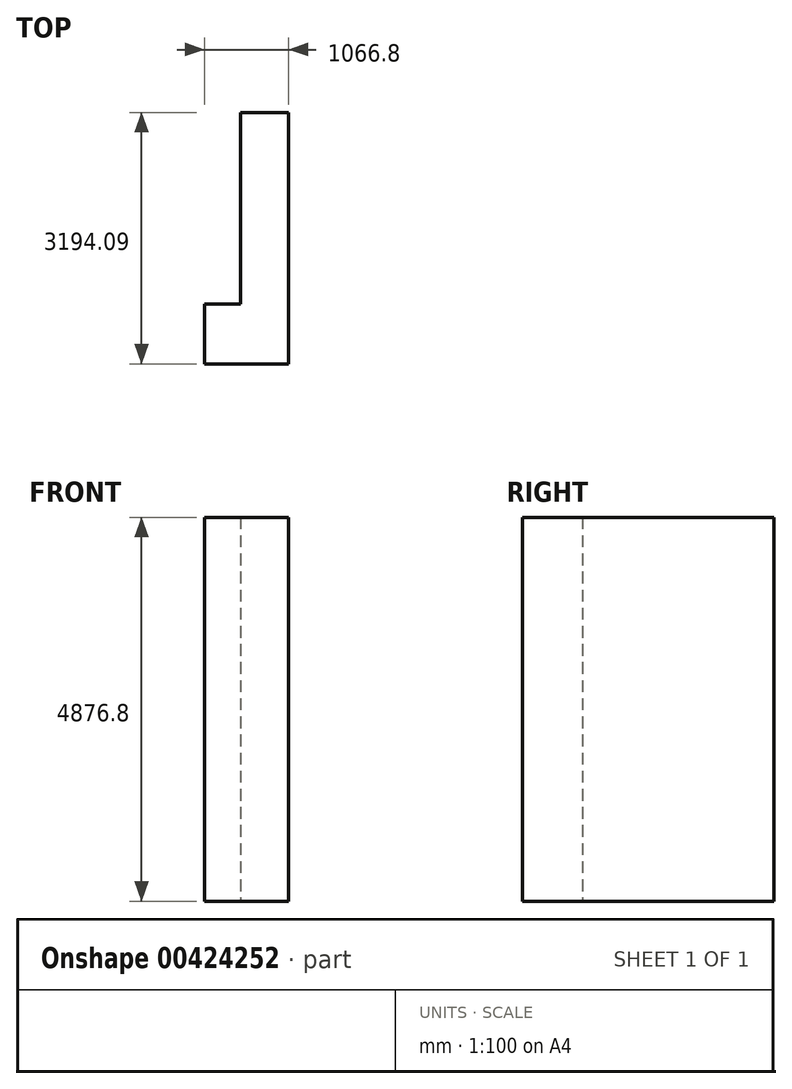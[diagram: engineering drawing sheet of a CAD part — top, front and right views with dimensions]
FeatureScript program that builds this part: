
annotation { "Feature Type Name" : "Feature", "Feature Type Description" : "" }
export const myFeature = defineFeature(function(context is Context, id is Id, definition is map)
    precondition{}
    {
        {
            var Q0;
            Q0=qCreatedBy(makeId("Top.planeOp"),FACE);
            var sketch = newSketch(context, id + "F0", { "sketchPlane" : qUnion([Q0])});
            skLineSegment(sketch, "E0", {"start": v(-5313.57, 0) * mm, "end": v(-5313.57, 1219.2) * mm});
            skLineSegment(sketch, "E1", {"start": v(-5313.57, 1219.2) * mm, "end": v(782.43, 1219.2) * mm});
            skLineSegment(sketch, "E2", {"start": v(782.43, 1219.2) * mm, "end": v(1849.23, 1219.2) * mm});
            skLineSegment(sketch, "E3", {"start": v(1849.23, 1219.2) * mm, "end": v(2763.63, 1219.2) * mm});
            skLineSegment(sketch, "E4", {"start": v(2763.63, 1219.2) * mm, "end": v(2763.63, 2590.8) * mm});
            skLineSegment(sketch, "E5", {"start": v(2763.63, 2590.8) * mm, "end": v(2763.63, 5334) * mm});
            skLineSegment(sketch, "E6", {"start": v(2763.63, 5334) * mm, "end": v(2763.63, 8686.8) * mm});
            skLineSegment(sketch, "E7", {"start": v(2763.63, 8686.8) * mm, "end": v(23794.83, 8686.8) * mm});
            skLineSegment(sketch, "E8", {"start": v(23794.83, 8686.8) * mm, "end": v(23794.83, 1219.2) * mm});
            skLineSegment(sketch, "E9", {"start": v(23794.83, 1219.2) * mm, "end": v(26233.23, 1219.2) * mm});
            skLineSegment(sketch, "E10", {"start": v(27300.03, 1219.2) * mm, "end": v(30348.03, 1219.2) * mm});
            skLineSegment(sketch, "E11", {"start": v(32634.03, -9296.4) * mm, "end": v(21439.84, -9296.4) * mm});
            skLineSegment(sketch, "E12", {"start": v(32634.03, -9296.4) * mm, "end": v(-5313.57, -9296.4) * mm});
            skLineSegment(sketch, "E13", {"start": v(-5313.57, -9296.4) * mm, "end": v(-5313.57, -8077.2) * mm});
            skLineSegment(sketch, "E14", {"start": v(-5313.57, -8077.2) * mm, "end": v(-5313.57, -6248.4) * mm});
            skLineSegment(sketch, "E15", {"start": v(-5313.57, -6248.4) * mm, "end": v(-5313.57, -3505.2) * mm});
            skLineSegment(sketch, "E16", {"start": v(-5313.57, -3505.2) * mm, "end": v(-10037.97, -3505.2) * mm});
            skLineSegment(sketch, "E17", {"start": v(30348.03, 1219.2) * mm, "end": v(31262.43, 1219.2) * mm});
            skLineSegment(sketch, "E18", {"start": v(-5313.57, 0) * mm, "end": v(-5313.57, -3505.2) * mm});
            skLineSegment(sketch, "E19", {"start": v(31872.03, 1219.2) * mm, "end": v(31262.43, 1219.2) * mm});
            skLineSegment(sketch, "E20", {"start": v(31872.03, 1219.2) * mm, "end": v(31872.03, 152.4) * mm});
            skLineSegment(sketch, "E21", {"start": v(31872.03, -1828.8) * mm, "end": v(31872.03, -6096) * mm});
            skLineSegment(sketch, "E22", {"start": v(-10037.97, -3505.2) * mm, "end": v(-10037.97, 0) * mm});
            skLineSegment(sketch, "E23", {"start": v(-10037.97, 0) * mm, "end": v(-9733.17, 0) * mm});
            skLineSegment(sketch, "E24", {"start": v(-9733.17, 0) * mm, "end": v(-9733.17, 914.4) * mm});
            skLineSegment(sketch, "E25", {"start": v(31872.03, -6096) * mm, "end": v(33091.23, -6096) * mm});
            skLineSegment(sketch, "E26", {"start": v(32634.03, -9296.4) * mm, "end": v(33091.23, -9296.4) * mm});
            skLineSegment(sketch, "E27", {"start": v(26233.23, 1219.2) * mm, "end": v(27300.03, 1219.2) * mm});
            skLineSegment(sketch, "E28.0", {"start": v(24556.83, 9448.8) * mm, "end": v(24556.83, 1676.4) * mm});
            skLineSegment(sketch, "E28.1", {"start": v(2154.03, 9448.8) * mm, "end": v(24556.83, 9448.8) * mm});
            skLineSegment(sketch, "E29.0", {"start": v(32634.03, 1676.4) * mm, "end": v(32634.03, 152.4) * mm});
            skLineSegment(sketch, "E30.0", {"start": v(32634.03, -1828.8) * mm, "end": v(32634.03, -5334) * mm});
            skLineSegment(sketch, "E31.0", {"start": v(32634.03, -5334) * mm, "end": v(33700.83, -5334) * mm});
            skLineSegment(sketch, "E32", {"start": v(31872.03, 152.4) * mm, "end": v(32634.03, 152.4) * mm});
            skLineSegment(sketch, "E33", {"start": v(31872.03, -1828.8) * mm, "end": v(32634.03, -1828.8) * mm});
            skLineSegment(sketch, "E34", {"start": v(32634.03, 152.4) * mm, "end": v(33624.63, 152.4) * mm});
            skLineSegment(sketch, "E35", {"start": v(32634.03, -1828.8) * mm, "end": v(33624.63, -1828.8) * mm});
            skArc(sketch, "E36", {"start": v(33624.63, 152.4) * mm, "mid": v(33334.49, -548.06) * mm, "end": v(32634.03, -838.2) * mm});
            skArc(sketch, "E37", {"start": v(33624.63, -1828.8) * mm, "mid": v(33334.49, -1128.34) * mm, "end": v(32634.03, -838.2) * mm});
            skLineSegment(sketch, "E38", {"start": v(32634.03, 152.4) * mm, "end": v(32634.03, -1828.8) * mm});
            skLineSegment(sketch, "E39.0", {"start": v(24556.83, 1676.4) * mm, "end": v(26233.23, 1676.4) * mm});
            skLineSegment(sketch, "E40.0", {"start": v(32634.03, -10058.4) * mm, "end": v(-5465.97, -10058.4) * mm});
            skLineSegment(sketch, "E41.0", {"start": v(2154.03, 5334) * mm, "end": v(2154.03, 9448.8) * mm});
            skLineSegment(sketch, "E42.0", {"start": v(-6227.97, 1676.4) * mm, "end": v(782.43, 1676.4) * mm});
            skLineSegment(sketch, "E43.0", {"start": v(1849.23, 1676.4) * mm, "end": v(2458.83, 1676.4) * mm});
            skLineSegment(sketch, "E44.0", {"start": v(2458.83, 1676.4) * mm, "end": v(2458.83, 2590.8) * mm});
            skLineSegment(sketch, "E45", {"start": v(782.43, 1676.4) * mm, "end": v(782.43, 1219.2) * mm});
            skLineSegment(sketch, "E46", {"start": v(1849.23, 1676.4) * mm, "end": v(1849.23, 1219.2) * mm});
            skLineSegment(sketch, "E47", {"start": v(2458.83, 2590.8) * mm, "end": v(2763.63, 2590.8) * mm});
            skLineSegment(sketch, "E48", {"start": v(2763.63, 5334) * mm, "end": v(2154.03, 5334) * mm});
            skLineSegment(sketch, "E49", {"start": v(26233.23, 1676.4) * mm, "end": v(26233.23, 1219.2) * mm});
            skLineSegment(sketch, "E50.0", {"start": v(27300.03, 1676.4) * mm, "end": v(30348.03, 1676.4) * mm});
            skLineSegment(sketch, "E51.0", {"start": v(32634.03, 1676.4) * mm, "end": v(31262.43, 1676.4) * mm});
            skLineSegment(sketch, "E52", {"start": v(30348.03, 1219.2) * mm, "end": v(30348.03, 1676.4) * mm});
            skLineSegment(sketch, "E53", {"start": v(31262.43, 1676.4) * mm, "end": v(31262.43, 1219.2) * mm});
            skLineSegment(sketch, "E54", {"start": v(27300.03, 1676.4) * mm, "end": v(27300.03, 1219.2) * mm});
            skLineSegment(sketch, "E55.0", {"start": v(33700.83, -5334) * mm, "end": v(33700.83, -6864.31) * mm});
            skLineSegment(sketch, "E56", {"start": v(33091.23, -6096) * mm, "end": v(33091.23, -9296.4) * mm});
            skLineSegment(sketch, "E57", {"start": v(33700.83, -6864.31) * mm, "end": v(33091.23, -6864.31) * mm});
            skLineSegment(sketch, "E58", {"start": v(32634.03, -9296.4) * mm, "end": v(32634.03, -10058.4) * mm});
            skLineSegment(sketch, "E59", {"start": v(32634.03, -10058.4) * mm, "end": v(33700.83, -10058.4) * mm});
            skLineSegment(sketch, "E60", {"start": v(33700.83, -6864.31) * mm, "end": v(33700.83, -10058.4) * mm});
            skLineSegment(sketch, "E61.0", {"start": v(-6227.97, 0) * mm, "end": v(-6227.97, 1676.4) * mm});
            skLineSegment(sketch, "E62", {"start": v(-6227.97, 0) * mm, "end": v(-5313.57, 0) * mm});
            skLineSegment(sketch, "E63.0", {"start": v(-5618.37, -6248.4) * mm, "end": v(-5618.37, -3810) * mm});
            skLineSegment(sketch, "E64.0", {"start": v(-5465.97, -10058.4) * mm, "end": v(-5465.97, -8077.2) * mm});
            skLineSegment(sketch, "E65", {"start": v(-5465.97, -8077.2) * mm, "end": v(-5313.57, -8077.2) * mm});
            skLineSegment(sketch, "E66.0", {"start": v(-5618.37, -3810) * mm, "end": v(-10342.77, -3810) * mm});
            skLineSegment(sketch, "E67.0", {"start": v(-10342.77, -3810) * mm, "end": v(-10342.77, 295.76) * mm});
            skLineSegment(sketch, "E68.0", {"start": v(-10342.77, 304.8) * mm, "end": v(-10037.97, 304.8) * mm});
            skLineSegment(sketch, "E69.0", {"start": v(-10037.97, 304.8) * mm, "end": v(-10037.97, 914.4) * mm});
            skLineSegment(sketch, "E70", {"start": v(-9733.17, 914.4) * mm, "end": v(-10037.97, 914.4) * mm});
            skLineSegment(sketch, "E71", {"start": v(-5618.37, -6248.4) * mm, "end": v(-5313.57, -6248.4) * mm});
            skLineSegment(sketch, "E72", {"start": v(-5313.57, -3505.2) * mm, "end": v(-5313.57, -6248.4) * mm});
            skLineSegment(sketch, "E73", {"start": v(-10342.77, -3810) * mm, "end": v(-5618.37, -3810) * mm});
            skLineSegment(sketch, "E74", {"start": v(-10037.97, -3505.2) * mm, "end": v(-5313.57, -3505.2) * mm});
            skLineSegment(sketch, "E75", {"start": v(-9733.17, 914.4) * mm, "end": v(-9733.17, 0) * mm});
            skLineSegment(sketch, "E76", {"start": v(-10037.97, 914.4) * mm, "end": v(-10037.97, 304.8) * mm});
            skLineSegment(sketch, "E77", {"start": v(-10342.77, 295.76) * mm, "end": v(-10037.97, 304.8) * mm});
            skSolve(sketch);
        }
        {
            var Q0;
            {var subQ2=sQuery(id+"F0.wireOp",EDGE,"E26");Q0=makeQuery(id+"F0.imprint","IMPRINT",FACE,{"disambiguationData":[TD([[makeQuery(id+"F0.imprint","IMPRINT",EDGE,{"derivedFrom":subQ2}),-1.0]])]});}
            extrude(context, id + "F1", {"entities" : qUnion([Q0]), "depth" : 4876.8 * mm});
        }
    });
